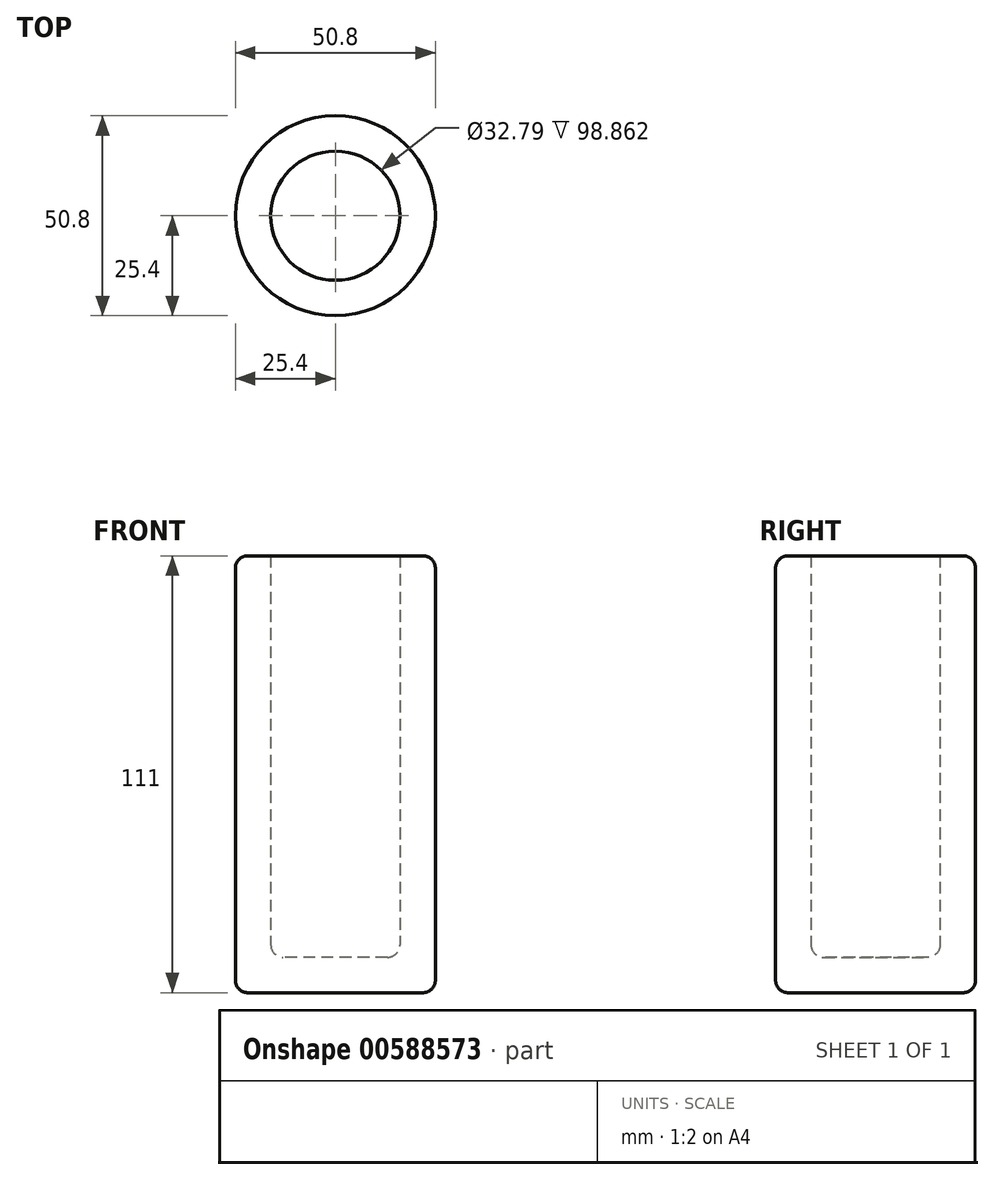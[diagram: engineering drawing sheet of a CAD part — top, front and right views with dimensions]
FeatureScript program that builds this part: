
annotation { "Feature Type Name" : "Feature", "Feature Type Description" : "" }
export const myFeature = defineFeature(function(context is Context, id is Id, definition is map)
    precondition{}
    {
        {
            var Q0;
            Q0=qCreatedBy(makeId("Top.planeOp"),FACE);
            var sketch = newSketch(context, id + "F0", { "sketchPlane" : qUnion([Q0])});
            skCircle(sketch, "E0", {"center": v(0, 0) * mm, "radius": 25.4 * mm});
            skSolve(sketch);
        }
        {
            var Q0;
            Q0=makeQuery(id+"F0.imprint","IMPRINT",FACE,{"disambiguationData":[TD([[makeQuery(id+"F0.imprint","IMPRINT",EDGE,{"derivedFrom":sQuery(id+"F0.wireOp",EDGE,"E0")}),1.0]])]});
            extrude(context, id + "F1", {"entities" : qUnion([Q0]), "depth" : 111 * mm, "offsetDistance" : 25.4 * mm});
        }
        {
            var Q0;
            Q0=makeQuery(id+"F1.opExtrude","CAP_FACE",FACE,{"disambiguationData":[OSD([sQuery(id+"F0.wireOp",EDGE,"E0")])],"isStart":false});
            shell(context, id + "F2", {"entities" : qUnion([Q0]), "thickness" : 9 * mm});
        }
        {
            var Q0;
            Q0=makeQuery(id+"F1.opExtrude","SWEPT_FACE",FACE,{"disambiguationData":[OSD([sQuery(id+"F0.wireOp",EDGE,"E0")])]});
            var Q1;
            {var subQ0=sQuery(id+"F0.wireOp",EDGE,"E0");Q1=makeQuery(id+"F2.opShell","OFFSET_EDGE",EDGE,{"disambiguationData":[OSD([subQ0]),TDD([makeQuery(id+"F1.opExtrude","CAP_EDGE",EDGE,{"disambiguationData":[OSD([subQ0])],"isStart":true})])]});}
            fillet(context, id + "F3", {"entities" : qUnion([Q0, Q1]), "radius" : 3.14 * mm, "tangentPropagation" : true, "allowEdgeOverflow" : false});
        }
    });
